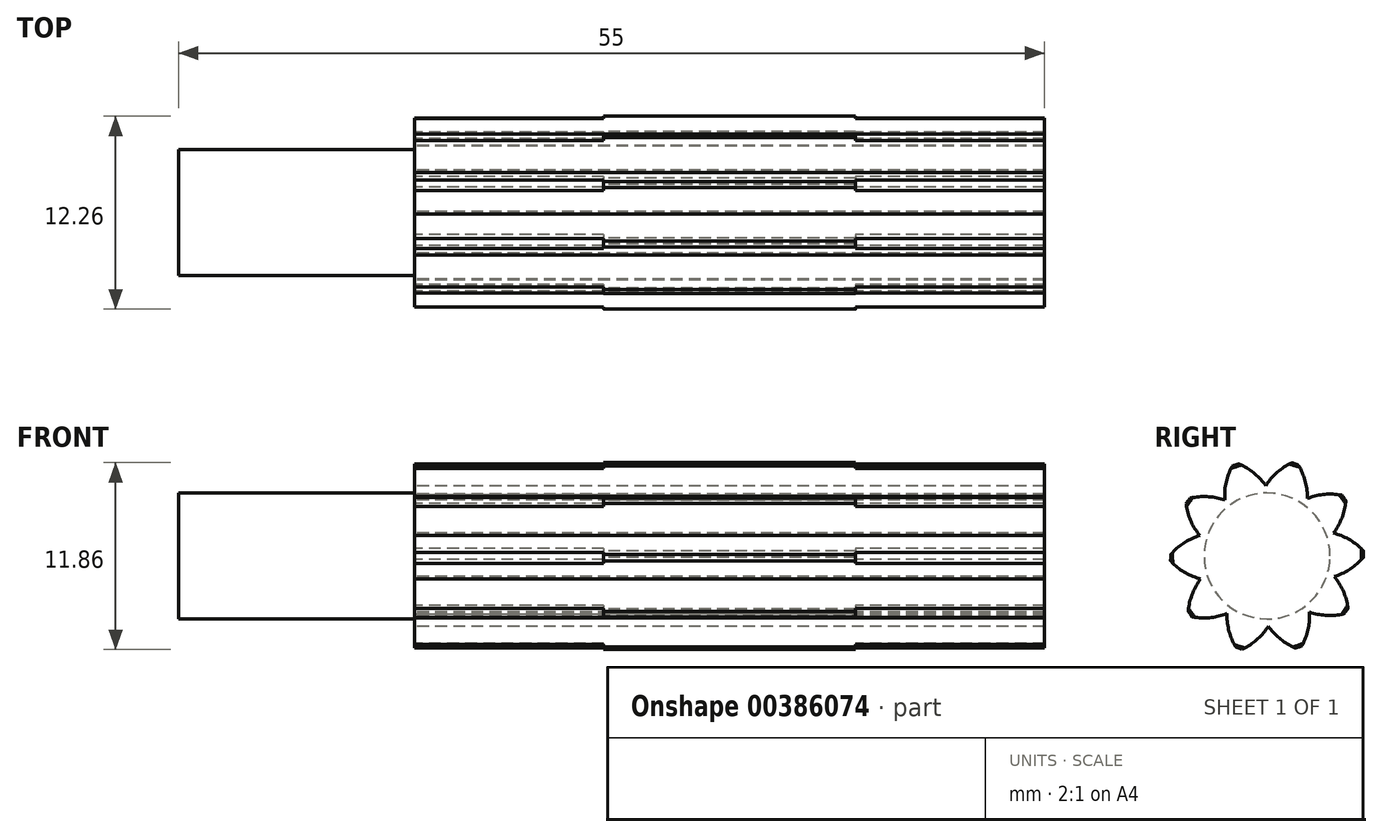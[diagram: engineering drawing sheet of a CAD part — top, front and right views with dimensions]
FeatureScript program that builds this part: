
annotation { "Feature Type Name" : "Feature", "Feature Type Description" : "" }
export const myFeature = defineFeature(function(context is Context, id is Id, definition is map)
    precondition{}
    {
        {
            var Q0;
            Q0=qCreatedBy(makeId("Front.planeOp"),FACE);
            var sketch = newSketch(context, id + "F0", { "sketchPlane" : qUnion([Q0])});
            skLineSegment(sketch, "E0", {"start": v(-71.62, 0) * mm, "end": v(71.98, 0) * mm});
            skLineSegment(sketch, "E1", {"start": v(0, 47.97) * mm, "end": v(0, -46.28) * mm});
            skLineSegment(sketch, "E2.bottom", {"start": v(-35, 0) * mm, "end": v(0, 0) * mm});
            skLineSegment(sketch, "E2.top", {"start": v(-35, 4) * mm, "end": v(0, 4) * mm});
            skLineSegment(sketch, "E2.left", {"start": v(-35, 0) * mm, "end": v(-35, 4) * mm});
            skLineSegment(sketch, "E2.right", {"start": v(0, 0) * mm, "end": v(0, 4) * mm});
            skLineSegment(sketch, "E3.bottom", {"start": v(-20, 0) * mm, "end": v(0, 0) * mm});
            skLineSegment(sketch, "E3.top", {"start": v(-20, 6) * mm, "end": v(0, 6) * mm});
            skLineSegment(sketch, "E3.left", {"start": v(-20, 0) * mm, "end": v(-20, 6) * mm});
            skLineSegment(sketch, "E3.right", {"start": v(0, 0) * mm, "end": v(0, 6) * mm});
            skLineSegment(sketch, "E4.bottom", {"start": v(-17.5, 0) * mm, "end": v(0, 0) * mm});
            skLineSegment(sketch, "E4.right", {"start": v(0, 0) * mm, "end": v(0, 7.5) * mm});
            skLineSegment(sketch, "E5.bottom", {"start": v(-8, 0) * mm, "end": v(0, 0) * mm});
            skLineSegment(sketch, "E5.top", {"start": v(-8, 7.5) * mm, "end": v(0, 7.5) * mm});
            skLineSegment(sketch, "E5.left", {"start": v(-8, 0) * mm, "end": v(-8, 7.5) * mm});
            skLineSegment(sketch, "E6.MirrorCS", {"start": v(0, 0) * mm, "end": v(0, -7.5) * mm});
            skLineSegment(sketch, "E7.MirrorCS", {"start": v(0, 0) * mm, "end": v(0, -4) * mm});
            skLineSegment(sketch, "E8.MirrorCS", {"start": v(0, 0) * mm, "end": v(0, -6) * mm});
            skLineSegment(sketch, "E9.MirrorCS", {"start": v(-20, -6) * mm, "end": v(0, -6) * mm});
            skLineSegment(sketch, "E10.MirrorCS", {"start": v(-8, 0) * mm, "end": v(-8, -7.5) * mm});
            skLineSegment(sketch, "E11.MirrorCS", {"start": v(-8, -7.5) * mm, "end": v(0, -7.5) * mm});
            skLineSegment(sketch, "E12.MirrorCS", {"start": v(-35, -4) * mm, "end": v(0, -4) * mm});
            skLineSegment(sketch, "E13.MirrorCS", {"start": v(-35, 0) * mm, "end": v(-35, -4) * mm});
            skLineSegment(sketch, "E14.MirrorCS", {"start": v(-20, 0) * mm, "end": v(-20, -6) * mm});
            skLineSegment(sketch, "E15.MirrorCS", {"start": v(8, 0) * mm, "end": v(0, 0) * mm});
            skLineSegment(sketch, "E16.MirrorCS", {"start": v(20, 0) * mm, "end": v(0, 0) * mm});
            skLineSegment(sketch, "E17.MirrorCS", {"start": v(17.5, 0) * mm, "end": v(0, 0) * mm});
            skLineSegment(sketch, "E18.MirrorCS", {"start": v(35, 0) * mm, "end": v(0, 0) * mm});
            skLineSegment(sketch, "E19.MirrorCS", {"start": v(35, 4) * mm, "end": v(0, 4) * mm});
            skLineSegment(sketch, "E20.MirrorCS", {"start": v(8, 0) * mm, "end": v(8, 7.5) * mm});
            skLineSegment(sketch, "E21.MirrorCS", {"start": v(8, 0) * mm, "end": v(8, -7.5) * mm});
            skLineSegment(sketch, "E22.MirrorCS", {"start": v(8, 7.5) * mm, "end": v(0, 7.5) * mm});
            skLineSegment(sketch, "E23.MirrorCS", {"start": v(35, 0) * mm, "end": v(35, 4) * mm});
            skLineSegment(sketch, "E24.MirrorCS", {"start": v(8, -7.5) * mm, "end": v(0, -7.5) * mm});
            skLineSegment(sketch, "E25.MirrorCS", {"start": v(35, -4) * mm, "end": v(0, -4) * mm});
            skLineSegment(sketch, "E26.MirrorCS", {"start": v(20, -6) * mm, "end": v(0, -6) * mm});
            skLineSegment(sketch, "E27.MirrorCS", {"start": v(20, 6) * mm, "end": v(0, 6) * mm});
            skLineSegment(sketch, "E28.MirrorCS", {"start": v(35, 0) * mm, "end": v(35, -4) * mm});
            skLineSegment(sketch, "E29.MirrorCS", {"start": v(20, 0) * mm, "end": v(20, 6) * mm});
            skLineSegment(sketch, "E30.MirrorCS", {"start": v(20, 0) * mm, "end": v(20, -6) * mm});
            skSolve(sketch);
        }
        {
            var Q0;
            {var subQ0=sQuery(id+"F0.wireOp",EDGE,"E2.left");Q0=makeQuery(id+"F0.imprint","IMPRINT",FACE,{"disambiguationData":[TD([[makeQuery(id+"F0.imprint","IMPRINT",EDGE,{"derivedFrom":subQ0}),-1.0]])]});}
            var Q1;
            {var subQ1=sQuery(id+"F0.wireOp",EDGE,"E3.left");var subQ7=sQuery(id+"F0.wireOp",EDGE,"E2.top");var subQ9=makeQuery(id+"F0.imprint","INTERSECT",VERTEX,{"derivedFrom":[subQ7,subQ1]});Q1=makeQuery(id+"F0.imprint","IMPRINT",FACE,{"disambiguationData":[TD([[makeQuery(id+"F0.imprint","IMPRINT",EDGE,{"disambiguationData":[TD([[subQ9,-1.0]])],"derivedFrom":subQ7}),-1.0]])]});}
            var Q2;
            {var subQ0=sQuery(id+"F0.wireOp",EDGE,"E3.left");var subQ1=sQuery(id+"F0.wireOp",EDGE,"E2.top");var subQ2=makeQuery(id+"F0.imprint","INTERSECT",VERTEX,{"derivedFrom":[subQ1,subQ0]});Q2=makeQuery(id+"F0.imprint","IMPRINT",FACE,{"disambiguationData":[TD([[makeQuery(id+"F0.imprint","IMPRINT",EDGE,{"disambiguationData":[TD([[subQ2,-1.0]])],"derivedFrom":subQ1}),1.0]])]});}
            var Q3;
            {var subQ5=sQuery(id+"F0.wireOp",EDGE,"E5.top");Q3=makeQuery(id+"F0.imprint","IMPRINT",FACE,{"disambiguationData":[TD([[makeQuery(id+"F0.imprint","IMPRINT",EDGE,{"derivedFrom":subQ5}),-1.0]])]});}
            var Q4;
            {var subQ1=sQuery(id+"F0.wireOp",EDGE,"E2.top");var subQ3=sQuery(id+"F0.wireOp",EDGE,"E5.left");var subQ4=makeQuery(id+"F0.imprint","INTERSECT",VERTEX,{"derivedFrom":[subQ1,subQ3]});Q4=makeQuery(id+"F0.imprint","IMPRINT",FACE,{"disambiguationData":[TD([[makeQuery(id+"F0.imprint","IMPRINT",EDGE,{"disambiguationData":[TD([[subQ4,-1.0]])],"derivedFrom":subQ1}),-1.0]])]});}
            var Q5;
            {var subQ3=sQuery(id+"F0.wireOp",EDGE,"E5.left");var subQ5=sQuery(id+"F0.wireOp",EDGE,"E3.top");var subQ7=makeQuery(id+"F0.imprint","INTERSECT",VERTEX,{"derivedFrom":[subQ5,subQ3]});Q5=makeQuery(id+"F0.imprint","IMPRINT",FACE,{"disambiguationData":[TD([[makeQuery(id+"F0.imprint","IMPRINT",EDGE,{"disambiguationData":[TD([[subQ7,1.0]])],"derivedFrom":subQ3}),-1.0]])]});}
            var Q6;
            {var subQ3=sQuery(id+"F0.wireOp",EDGE,"E20.MirrorCS");var subQ5=sQuery(id+"F0.wireOp",EDGE,"E27.MirrorCS");var subQ7=makeQuery(id+"F0.imprint","INTERSECT",VERTEX,{"derivedFrom":[subQ3,subQ5]});Q6=makeQuery(id+"F0.imprint","IMPRINT",FACE,{"disambiguationData":[TD([[makeQuery(id+"F0.imprint","IMPRINT",EDGE,{"disambiguationData":[TD([[subQ7,1.0]])],"derivedFrom":subQ3}),1.0]])]});}
            var Q7;
            {var subQ0=sQuery(id+"F0.wireOp",EDGE,"E29.MirrorCS");var subQ1=sQuery(id+"F0.wireOp",EDGE,"E19.MirrorCS");var subQ2=makeQuery(id+"F0.imprint","INTERSECT",VERTEX,{"derivedFrom":[subQ1,subQ0]});Q7=makeQuery(id+"F0.imprint","IMPRINT",FACE,{"disambiguationData":[TD([[makeQuery(id+"F0.imprint","IMPRINT",EDGE,{"disambiguationData":[TD([[subQ2,-1.0]])],"derivedFrom":subQ1}),-1.0]])]});}
            var Q8;
            {var subQ0=sQuery(id+"F0.wireOp",EDGE,"E22.MirrorCS");Q8=makeQuery(id+"F0.imprint","IMPRINT",FACE,{"disambiguationData":[TD([[makeQuery(id+"F0.imprint","IMPRINT",EDGE,{"derivedFrom":subQ0}),1.0]])]});}
            var Q9;
            {var subQ0=sQuery(id+"F0.wireOp",EDGE,"E18.MirrorCS");Q9=makeQuery(id+"F0.imprint","IMPRINT",FACE,{"disambiguationData":[TD([[makeQuery(id+"F0.imprint","IMPRINT",EDGE,{"derivedFrom":subQ0}),-1.0]])]});}
            var Q10;
            {var subQ1=sQuery(id+"F0.wireOp",EDGE,"E19.MirrorCS");var subQ3=sQuery(id+"F0.wireOp",EDGE,"E20.MirrorCS");var subQ4=makeQuery(id+"F0.imprint","INTERSECT",VERTEX,{"derivedFrom":[subQ1,subQ3]});Q10=makeQuery(id+"F0.imprint","IMPRINT",FACE,{"disambiguationData":[TD([[makeQuery(id+"F0.imprint","IMPRINT",EDGE,{"disambiguationData":[TD([[subQ4,-1.0]])],"derivedFrom":subQ1}),1.0]])]});}
            var Q11;
            {var subQ4=sQuery(id+"F0.wireOp",EDGE,"E29.MirrorCS");var subQ6=sQuery(id+"F0.wireOp",EDGE,"E19.MirrorCS");var subQ8=makeQuery(id+"F0.imprint","INTERSECT",VERTEX,{"derivedFrom":[subQ6,subQ4]});Q11=makeQuery(id+"F0.imprint","IMPRINT",FACE,{"disambiguationData":[TD([[makeQuery(id+"F0.imprint","IMPRINT",EDGE,{"disambiguationData":[TD([[subQ8,-1.0]])],"derivedFrom":subQ6}),1.0]])]});}
            var Q12;
            Q12=sQuery(id+"F0.wireOp",EDGE,"E0");
            revolve(context, id + "F1", {"entities" : qUnion([Q0, Q1, Q2, Q3, Q4, Q5, Q6, Q7, Q8, Q9, Q10, Q11]), "axis" : qUnion([Q12]), "revolveType" : RevolveType.FULL});
        }
        {
            var Q0;
            Q0=makeQuery(id+"F1.opRevolve","SWEPT_FACE",FACE,{"disambiguationData":[OSD([sQuery(id+"F0.wireOp",EDGE,"E3.left")])]});
            var sketch = newSketch(context, id + "F2", { "sketchPlane" : qUnion([Q0])});
            skLineSegment(sketch, "E31", {"start": v(0.1, 9.69) * mm, "end": v(0.1, -9.3) * mm, "construction": true});
            skLineSegment(sketch, "E32", {"start": v(5, 9.52) * mm, "end": v(5, -9.47) * mm, "construction": true});
            skCircle(sketch, "E33", {"center": v(10, 0) * mm, "radius": 5 * mm, "construction": true});
            skCircle(sketch, "E34", {"center": v(10, 0) * mm, "radius": 4 * mm, "construction": true});
            skCircle(sketch, "E35", {"center": v(10, 0) * mm, "radius": 6 * mm, "construction": true});
            skCircle(sketch, "E36.MirrorC", {"center": v(0, 0) * mm, "radius": 5 * mm, "construction": true});
            skCircle(sketch, "E37.MirrorC", {"center": v(0, 0) * mm, "radius": 4 * mm, "construction": true});
            skCircle(sketch, "E38.MirrorC", {"center": v(0, 0) * mm, "radius": 6 * mm, "construction": true});
            skLineSegment(sketch, "E39", {"start": v(0, 0) * mm, "end": v(10, 0) * mm, "construction": true});
            skLineSegment(sketch, "E40", {"start": v(2.25, 3.82) * mm, "end": v(5.03, -0.3) * mm, "construction": true});
            skLineSegment(sketch, "E41", {"start": v(5.03, -0.3) * mm, "end": v(8.51, -4.44) * mm, "construction": true});
            skLineSegment(sketch, "E42", {"start": v(5.03, -0.3) * mm, "end": v(2.13, -3.64) * mm, "construction": true});
            skArc(sketch, "E43", {"start": v(3.87, 1.41) * mm, "mid": v(5.1, 0.94) * mm, "end": v(6.12, 0.1) * mm});
            skArc(sketch, "E44", {"start": v(3.87, 1.41) * mm, "mid": v(3.8, 1.43) * mm, "end": v(3.73, 1.44) * mm});
            skArc(sketch, "E45", {"start": v(6.12, 0.1) * mm, "mid": v(6.12, -0.1) * mm, "end": v(6.13, -0.31) * mm});
            skArc(sketch, "E46", {"start": v(6.13, -0.31) * mm, "mid": v(5.03, -1.15) * mm, "end": v(3.7, -1.54) * mm});
            skLineSegment(sketch, "E47.1.0", {"start": v(-5.6, 7.9) * mm, "end": v(5.56, -7.47) * mm, "construction": true});
            skArc(sketch, "E47.1.1", {"start": v(5.14, 3.35) * mm, "mid": v(4.74, 2.02) * mm, "end": v(3.9, 0.92) * mm});
            skArc(sketch, "E47.1.2", {"start": v(4.9, 3.68) * mm, "mid": v(5.01, 3.51) * mm, "end": v(5.14, 3.35) * mm});
            skArc(sketch, "E47.1.3", {"start": v(2.3, 3.42) * mm, "mid": v(3.58, 3.76) * mm, "end": v(4.9, 3.68) * mm});
            skLineSegment(sketch, "E47.2.0", {"start": v(-9.18, 3.1) * mm, "end": v(8.88, -2.78) * mm, "construction": true});
            skArc(sketch, "E47.2.1", {"start": v(2.2, 5.73) * mm, "mid": v(2.65, 4.42) * mm, "end": v(2.6, 3.03) * mm});
            skArc(sketch, "E47.2.2", {"start": v(1.8, 5.85) * mm, "mid": v(2, 5.79) * mm, "end": v(2.2, 5.73) * mm});
            skArc(sketch, "E47.2.3", {"start": v(-0.15, 4.12) * mm, "mid": v(0.69, 5.14) * mm, "end": v(1.8, 5.85) * mm});
            skLineSegment(sketch, "E47.3.0", {"start": v(-9.24, -2.9) * mm, "end": v(8.82, 2.98) * mm, "construction": true});
            skArc(sketch, "E47.3.1", {"start": v(-1.6, 5.93) * mm, "mid": v(-0.46, 5.14) * mm, "end": v(0.32, 3.99) * mm});
            skArc(sketch, "E47.3.2", {"start": v(-1.98, 5.79) * mm, "mid": v(-1.79, 5.85) * mm, "end": v(-1.6, 5.93) * mm});
            skArc(sketch, "E47.3.3", {"start": v(-2.54, 3.25) * mm, "mid": v(-2.47, 4.56) * mm, "end": v(-1.98, 5.79) * mm});
            skLineSegment(sketch, "E47.4.0", {"start": v(-5.78, -7.77) * mm, "end": v(5.38, 7.6) * mm, "construction": true});
            skArc(sketch, "E47.4.1", {"start": v(-4.78, 3.85) * mm, "mid": v(-3.39, 3.89) * mm, "end": v(-2.08, 3.42) * mm});
            skArc(sketch, "E47.4.2", {"start": v(-5, 3.52) * mm, "mid": v(-4.89, 3.68) * mm, "end": v(-4.78, 3.85) * mm});
            skArc(sketch, "E47.4.3", {"start": v(-3.96, 1.13) * mm, "mid": v(-4.68, 2.24) * mm, "end": v(-5, 3.52) * mm});
            skLineSegment(sketch, "E47.5.0", {"start": v(-0.1, -9.69) * mm, "end": v(-0.1, 9.3) * mm, "construction": true});
            skArc(sketch, "E47.5.1", {"start": v(-6.13, 0.31) * mm, "mid": v(-5.03, 1.15) * mm, "end": v(-3.7, 1.54) * mm});
            skArc(sketch, "E47.5.2", {"start": v(-6.12, -0.1) * mm, "mid": v(-6.12, 0.1) * mm, "end": v(-6.13, 0.31) * mm});
            skArc(sketch, "E47.5.3", {"start": v(-3.87, -1.41) * mm, "mid": v(-5.1, -0.94) * mm, "end": v(-6.12, -0.1) * mm});
            skLineSegment(sketch, "E47.6.0", {"start": v(5.6, -7.9) * mm, "end": v(-5.56, 7.47) * mm, "construction": true});
            skArc(sketch, "E47.6.1", {"start": v(-5.14, -3.35) * mm, "mid": v(-4.74, -2.02) * mm, "end": v(-3.9, -0.92) * mm});
            skArc(sketch, "E47.6.2", {"start": v(-4.9, -3.68) * mm, "mid": v(-5.01, -3.51) * mm, "end": v(-5.14, -3.35) * mm});
            skArc(sketch, "E47.6.3", {"start": v(-2.3, -3.42) * mm, "mid": v(-3.58, -3.76) * mm, "end": v(-4.9, -3.68) * mm});
            skLineSegment(sketch, "E47.7.0", {"start": v(9.18, -3.1) * mm, "end": v(-8.88, 2.78) * mm, "construction": true});
            skArc(sketch, "E47.7.1", {"start": v(-2.2, -5.73) * mm, "mid": v(-2.65, -4.42) * mm, "end": v(-2.6, -3.03) * mm});
            skArc(sketch, "E47.7.2", {"start": v(-1.8, -5.85) * mm, "mid": v(-2, -5.79) * mm, "end": v(-2.2, -5.73) * mm});
            skArc(sketch, "E47.7.3", {"start": v(0.15, -4.12) * mm, "mid": v(-0.69, -5.14) * mm, "end": v(-1.8, -5.85) * mm});
            skLineSegment(sketch, "E47.8.0", {"start": v(9.24, 2.9) * mm, "end": v(-8.82, -2.98) * mm, "construction": true});
            skArc(sketch, "E47.8.1", {"start": v(1.6, -5.93) * mm, "mid": v(0.46, -5.14) * mm, "end": v(-0.32, -3.99) * mm});
            skArc(sketch, "E47.8.2", {"start": v(1.98, -5.79) * mm, "mid": v(1.79, -5.85) * mm, "end": v(1.6, -5.93) * mm});
            skArc(sketch, "E47.8.3", {"start": v(2.54, -3.25) * mm, "mid": v(2.47, -4.56) * mm, "end": v(1.98, -5.79) * mm});
            skLineSegment(sketch, "E47.9.0", {"start": v(5.78, 7.77) * mm, "end": v(-5.38, -7.6) * mm, "construction": true});
            skArc(sketch, "E47.9.1", {"start": v(4.78, -3.85) * mm, "mid": v(3.39, -3.89) * mm, "end": v(2.08, -3.42) * mm});
            skArc(sketch, "E47.9.2", {"start": v(5, -3.52) * mm, "mid": v(4.89, -3.68) * mm, "end": v(4.78, -3.85) * mm});
            skArc(sketch, "E47.9.3", {"start": v(3.96, -1.13) * mm, "mid": v(4.68, -2.24) * mm, "end": v(5, -3.52) * mm});
            skSolve(sketch);
        }
        {
            var Q0;
            Q0 = qSketchRegion(id + "F2", true);
            extrude(context, id + "F3", {"entities" : qUnion([Q0]), "operationType" : NewBodyOperationType.INTERSECT, "endBound" : BoundingType.THROUGH_ALL, "oppositeDirection" : true, "depth" : 25 * mm, "hasSecondDirection" : true, "secondDirectionOppositeDirection" : false, "secondDirectionDepth" : 25 * mm});
        }
    });
